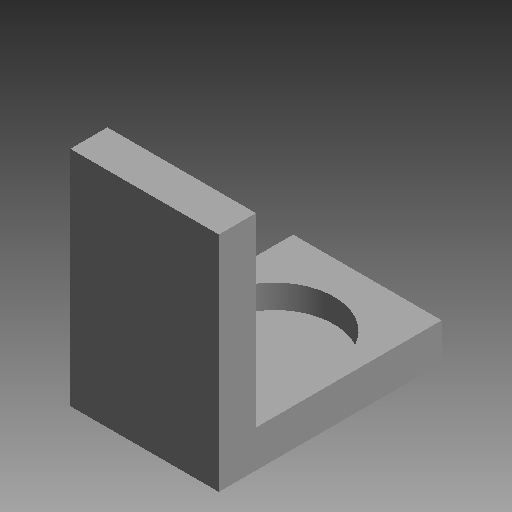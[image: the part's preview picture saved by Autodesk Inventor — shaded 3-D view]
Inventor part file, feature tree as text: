
AUTODESK INVENTOR PART (.ipt)
format: ipt  version: 2019 (Build 230136000, 136)  size: 76,288 bytes
history: native  units: mm (DEFAULTED — no unit token found)
features: other x3, sketch x2
ambient origin geometry x8: Origin, YZ Plane, XZ Plane, XY Plane, X Axis, Y Axis, Z Axis, Center Point
bodies: Solid1 (feature_tree)
feature tree (5):
  other  "spring tab for on arm"
  other  "Solid1::spring tab for on arm"
  other  "TaggingFeature1"
  sketch  "Sketch1"  dims[d0=10.0mm]
  sketch  "Sketch3"
